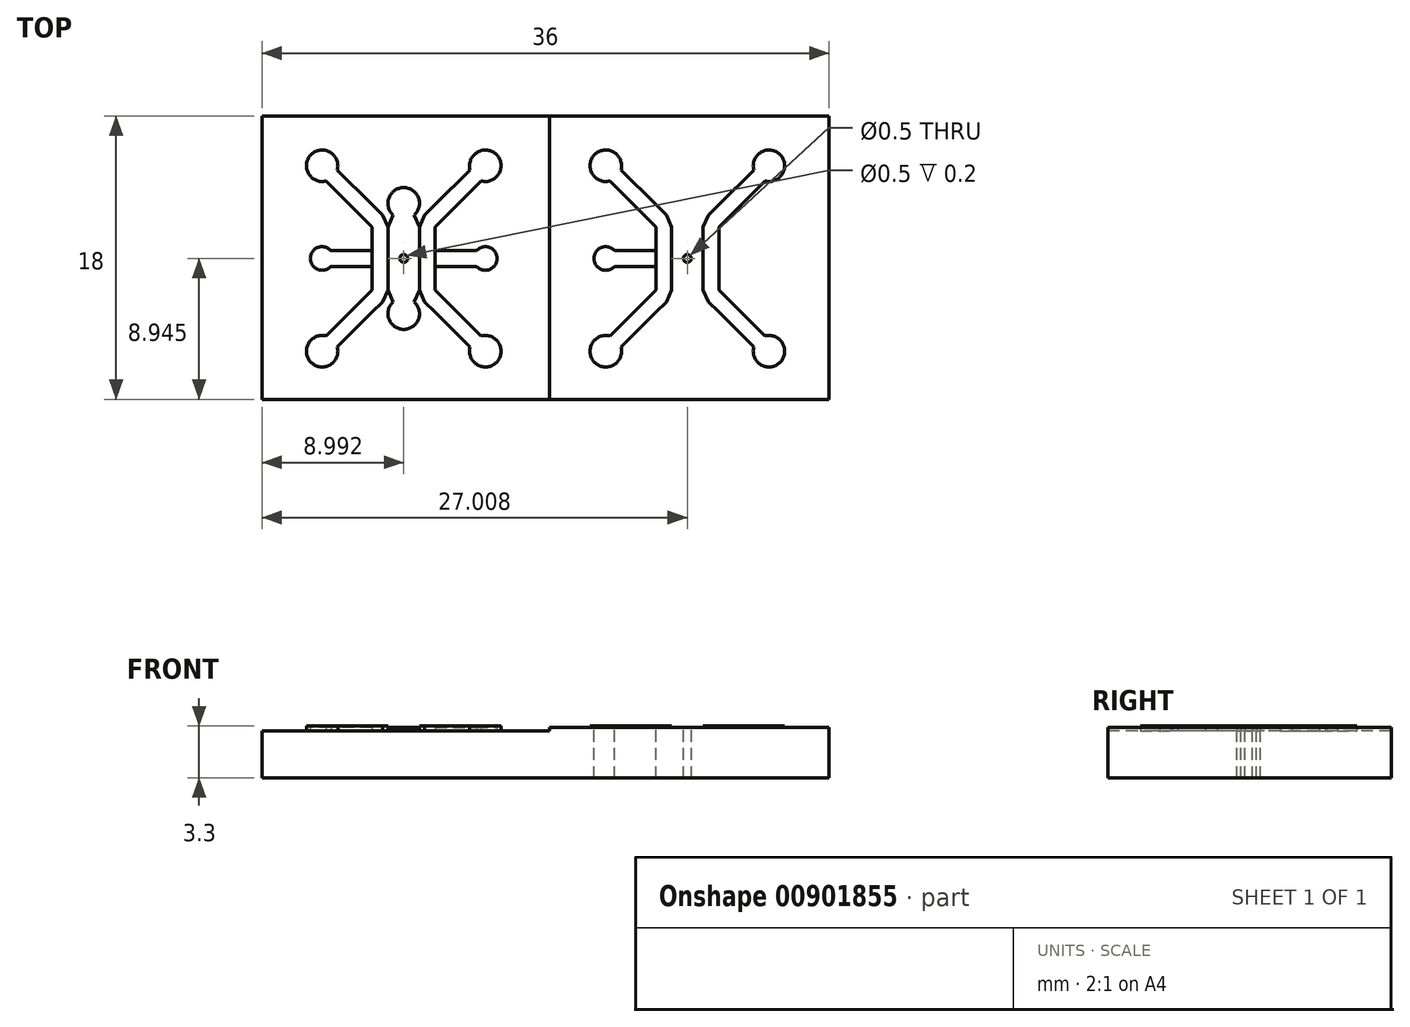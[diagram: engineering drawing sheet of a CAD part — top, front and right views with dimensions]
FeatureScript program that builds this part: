
annotation { "Feature Type Name" : "Feature", "Feature Type Description" : "" }
export const myFeature = defineFeature(function(context is Context, id is Id, definition is map)
    precondition{}
    {
        {
            var Q0;
            Q0=qCreatedBy(makeId("Top.planeOp"),FACE);
            var sketch = newSketch(context, id + "F0", { "sketchPlane" : qUnion([Q0])});
            skLineSegment(sketch, "E0.right", {"start": v(10, 8.95) * mm, "end": v(10, 10.95) * mm});
            skLineSegment(sketch, "E1.MirrorCS", {"start": v(8, 8.95) * mm, "end": v(8, 10.95) * mm});
            skLineSegment(sketch, "E2.MirrorCS", {"start": v(10, 8.95) * mm, "end": v(10, 6.95) * mm});
            skLineSegment(sketch, "E3.MirrorCS", {"start": v(8, 8.95) * mm, "end": v(8, 6.95) * mm});
            skLineSegment(sketch, "E4", {"start": v(9.65, 6.2) * mm, "end": v(10, 6.95) * mm});
            skLineSegment(sketch, "E5", {"start": v(8, 6.95) * mm, "end": v(8.33, 6.2) * mm});
            skCircle(sketch, "E6", {"center": v(9, 8.95) * mm, "radius": 0.25 * mm});
            skArc(sketch, "E7", {"start": v(8.33, 6.2) * mm, "mid": v(9, 4.45) * mm, "end": v(9.65, 6.2) * mm});
            skLineSegment(sketch, "E8.left", {"start": v(10, 10.95) * mm, "end": v(10, 8.95) * mm});
            skLineSegment(sketch, "E8.right", {"start": v(11, 10.95) * mm, "end": v(11, 8.95) * mm});
            skLineSegment(sketch, "E9.MirrorCS", {"start": v(11, 6.95) * mm, "end": v(11, 8.95) * mm});
            skLineSegment(sketch, "E10", {"start": v(10, 6.95) * mm, "end": v(10.33, 6.2) * mm});
            skLineSegment(sketch, "E11", {"start": v(10.33, 6.2) * mm, "end": v(11, 5.53) * mm});
            skLineSegment(sketch, "E12", {"start": v(11, 5.53) * mm, "end": v(13.2, 3.32) * mm});
            skArc(sketch, "E13", {"start": v(13.2, 3.32) * mm, "mid": v(14.88, 2.35) * mm, "end": v(13.92, 4.02) * mm});
            skArc(sketch, "E14.MirrorCS", {"start": v(8.33, 11.7) * mm, "mid": v(9, 13.45) * mm, "end": v(9.65, 11.7) * mm});
            skLineSegment(sketch, "E15.MirrorCS", {"start": v(9.65, 11.7) * mm, "end": v(10, 10.95) * mm});
            skLineSegment(sketch, "E16.MirrorCS", {"start": v(8, 10.95) * mm, "end": v(8.33, 11.7) * mm});
            skLineSegment(sketch, "E17.MirrorCS", {"start": v(10, 10.95) * mm, "end": v(10.33, 11.7) * mm});
            skLineSegment(sketch, "E18.MirrorCS", {"start": v(10.33, 11.7) * mm, "end": v(11, 12.36) * mm});
            skLineSegment(sketch, "E19.MirrorCS", {"start": v(11, 12.36) * mm, "end": v(13.2, 14.58) * mm});
            skArc(sketch, "E20.MirrorCS", {"start": v(13.2, 14.58) * mm, "mid": v(14.88, 15.54) * mm, "end": v(13.92, 13.87) * mm});
            skLineSegment(sketch, "E21", {"start": v(11, 6.95) * mm, "end": v(13.92, 4.02) * mm});
            skLineSegment(sketch, "E22.MirrorCS", {"start": v(11, 10.95) * mm, "end": v(13.92, 13.87) * mm});
            skLineSegment(sketch, "E23.MirrorCS", {"start": v(8, 10.95) * mm, "end": v(7.65, 11.7) * mm});
            skLineSegment(sketch, "E24.MirrorCS", {"start": v(8, 6.95) * mm, "end": v(7.65, 6.2) * mm});
            skLineSegment(sketch, "E25.MirrorCS", {"start": v(7.65, 11.7) * mm, "end": v(7, 12.36) * mm});
            skLineSegment(sketch, "E26.MirrorCS", {"start": v(7, 12.36) * mm, "end": v(4.78, 14.58) * mm});
            skArc(sketch, "E27.MirrorCS", {"start": v(4.78, 14.58) * mm, "mid": v(3.1, 15.54) * mm, "end": v(4.07, 13.87) * mm});
            skLineSegment(sketch, "E28.MirrorCS", {"start": v(7, 10.95) * mm, "end": v(4.07, 13.87) * mm});
            skLineSegment(sketch, "E29.MirrorCS", {"start": v(7, 10.95) * mm, "end": v(7, 8.95) * mm});
            skLineSegment(sketch, "E30.MirrorCS", {"start": v(7, 6.95) * mm, "end": v(7, 8.95) * mm});
            skArc(sketch, "E31.MirrorCS", {"start": v(4.78, 3.32) * mm, "mid": v(3.1, 2.35) * mm, "end": v(4.07, 4.02) * mm});
            skLineSegment(sketch, "E32.MirrorCS", {"start": v(7, 6.95) * mm, "end": v(4.07, 4.02) * mm});
            skLineSegment(sketch, "E33.MirrorCS", {"start": v(7, 5.53) * mm, "end": v(4.78, 3.32) * mm});
            skLineSegment(sketch, "E34.MirrorCS", {"start": v(7.65, 6.2) * mm, "end": v(7, 5.53) * mm});
            skLineSegment(sketch, "E35", {"start": v(11, 9.45) * mm, "end": v(13.61, 9.45) * mm});
            skLineSegment(sketch, "E36", {"start": v(11, 8.45) * mm, "end": v(13.61, 8.45) * mm});
            skArc(sketch, "E37", {"start": v(13.8, 9.6) * mm, "mid": v(13.7, 9.53) * mm, "end": v(13.61, 9.45) * mm});
            skArc(sketch, "E38", {"start": v(13.61, 8.45) * mm, "mid": v(14.91, 8.82) * mm, "end": v(13.8, 9.6) * mm});
            skLineSegment(sketch, "E39.MirrorCS", {"start": v(7, 9.45) * mm, "end": v(4.37, 9.45) * mm});
            skLineSegment(sketch, "E40.MirrorCS", {"start": v(7, 8.45) * mm, "end": v(4.37, 8.45) * mm});
            skArc(sketch, "E41.MirrorCS", {"start": v(4.37, 8.45) * mm, "mid": v(3.07, 8.82) * mm, "end": v(4.18, 9.6) * mm});
            skArc(sketch, "E42.MirrorCS", {"start": v(4.18, 9.6) * mm, "mid": v(4.28, 9.53) * mm, "end": v(4.37, 9.45) * mm});
            skPoint(sketch, "E43.startSnap0", {"position": v(15, 8.95) * mm});
            skPoint(sketch, "E43.startSnap1", {"position": v(14.91, 8.82) * mm});
            skPoint(sketch, "E43.endSnap0", {"position": v(14.91, 8.82) * mm});
            skPoint(sketch, "E44.visualSharp", {"position": v(0, 18) * mm});
            skPoint(sketch, "E45.visualSharp", {"position": v(0, 0) * mm});
            skLineSegment(sketch, "E46", {"start": v(9, 12.45) * mm, "end": v(9, 5.45) * mm});
            skLineSegment(sketch, "E47.bottom", {"start": v(0, 18) * mm, "end": v(18, 18) * mm});
            skLineSegment(sketch, "E47.top", {"start": v(0, 0) * mm, "end": v(18, 0) * mm});
            skLineSegment(sketch, "E47.left", {"start": v(0, 18) * mm, "end": v(0, 0) * mm});
            skLineSegment(sketch, "E47.right", {"start": v(18, 18) * mm, "end": v(18, 0) * mm});
            skLineSegment(sketch, "E48", {"start": v(21.4, 0) * mm, "end": v(21.4, 0) * mm});
            skLineSegment(sketch, "E49.MirrorCS", {"start": v(36, 18) * mm, "end": v(36, 0) * mm});
            skPoint(sketch, "E50.MirrorP", {"position": v(36, 0) * mm});
            skLineSegment(sketch, "E51.MirrorCS", {"start": v(36, 18) * mm, "end": v(18, 18) * mm});
            skPoint(sketch, "E52.MirrorP", {"position": v(36, 18) * mm});
            skLineSegment(sketch, "E53.MirrorCS", {"start": v(14.6, 0) * mm, "end": v(14.6, 0) * mm});
            skLineSegment(sketch, "E54.MirrorCS", {"start": v(36, 0) * mm, "end": v(18, 0) * mm});
            skPoint(sketch, "E55.MirrorP", {"position": v(21.09, 8.82) * mm});
            skLineSegment(sketch, "E56.MirrorCS", {"start": v(28, 10.95) * mm, "end": v(27.67, 11.7) * mm});
            skLineSegment(sketch, "E57.MirrorCS", {"start": v(26, 6.95) * mm, "end": v(25.67, 6.2) * mm});
            skLineSegment(sketch, "E58.MirrorCS", {"start": v(26, 8.95) * mm, "end": v(26, 10.95) * mm});
            skLineSegment(sketch, "E59.MirrorCS", {"start": v(28.35, 6.2) * mm, "end": v(29, 5.53) * mm});
            skArc(sketch, "E60.MirrorCS", {"start": v(31.82, 9.6) * mm, "mid": v(31.72, 9.53) * mm, "end": v(31.63, 9.45) * mm});
            skArc(sketch, "E61.MirrorCS", {"start": v(22.2, 9.6) * mm, "mid": v(22.3, 9.53) * mm, "end": v(22.39, 9.45) * mm});
            skLineSegment(sketch, "E62.MirrorCS", {"start": v(25.67, 11.7) * mm, "end": v(25, 12.36) * mm});
            skLineSegment(sketch, "E63.MirrorCS", {"start": v(28, 10.95) * mm, "end": v(28.35, 11.7) * mm});
            skLineSegment(sketch, "E64.MirrorCS", {"start": v(26, 10.95) * mm, "end": v(25.67, 11.7) * mm});
            skLineSegment(sketch, "E65.MirrorCS", {"start": v(26.35, 11.7) * mm, "end": v(26, 10.95) * mm});
            skLineSegment(sketch, "E66.MirrorCS", {"start": v(28.35, 11.7) * mm, "end": v(29, 12.36) * mm});
            skLineSegment(sketch, "E67.MirrorCS", {"start": v(25.67, 6.2) * mm, "end": v(25, 5.53) * mm});
            skLineSegment(sketch, "E68.MirrorCS", {"start": v(28, 6.95) * mm, "end": v(27.67, 6.2) * mm});
            skLineSegment(sketch, "E69.MirrorCS", {"start": v(28, 6.95) * mm, "end": v(28.35, 6.2) * mm});
            skArc(sketch, "E70.MirrorCS", {"start": v(22.39, 8.45) * mm, "mid": v(21.09, 8.82) * mm, "end": v(22.2, 9.6) * mm});
            skLineSegment(sketch, "E71.MirrorCS", {"start": v(26.35, 6.2) * mm, "end": v(26, 6.95) * mm});
            skPoint(sketch, "E72.MirrorP", {"position": v(21, 8.95) * mm});
            skCircle(sketch, "E73.MirrorC", {"center": v(27, 8.95) * mm, "radius": 0.25 * mm});
            skLineSegment(sketch, "E74.MirrorCS", {"start": v(28, 8.95) * mm, "end": v(28, 10.95) * mm});
            skArc(sketch, "E75.MirrorCS", {"start": v(22.8, 14.58) * mm, "mid": v(21.12, 15.54) * mm, "end": v(22.08, 13.87) * mm});
            skLineSegment(sketch, "E76.MirrorCS", {"start": v(29, 9.45) * mm, "end": v(31.63, 9.45) * mm});
            skLineSegment(sketch, "E77.MirrorCS", {"start": v(29, 6.95) * mm, "end": v(31.93, 4.02) * mm});
            skLineSegment(sketch, "E78.MirrorCS", {"start": v(25, 5.53) * mm, "end": v(22.8, 3.32) * mm});
            skLineSegment(sketch, "E79.MirrorCS", {"start": v(27, 12.45) * mm, "end": v(27, 5.45) * mm});
            skLineSegment(sketch, "E80.MirrorCS", {"start": v(29, 12.36) * mm, "end": v(31.22, 14.58) * mm});
            skLineSegment(sketch, "E81.MirrorCS", {"start": v(29, 6.95) * mm, "end": v(29, 8.95) * mm});
            skLineSegment(sketch, "E82.MirrorCS", {"start": v(29, 5.53) * mm, "end": v(31.22, 3.32) * mm});
            skLineSegment(sketch, "E83.MirrorCS", {"start": v(29, 8.45) * mm, "end": v(31.63, 8.45) * mm});
            skLineSegment(sketch, "E84.MirrorCS", {"start": v(29, 10.95) * mm, "end": v(29, 8.95) * mm});
            skLineSegment(sketch, "E85.MirrorCS", {"start": v(25, 12.36) * mm, "end": v(22.8, 14.58) * mm});
            skLineSegment(sketch, "E86.MirrorCS", {"start": v(26, 10.95) * mm, "end": v(26, 8.95) * mm});
            skArc(sketch, "E87.MirrorCS", {"start": v(31.63, 8.45) * mm, "mid": v(32.93, 8.82) * mm, "end": v(31.82, 9.6) * mm});
            skLineSegment(sketch, "E88.MirrorCS", {"start": v(29, 10.95) * mm, "end": v(31.93, 13.87) * mm});
            skLineSegment(sketch, "E89.MirrorCS", {"start": v(28, 8.95) * mm, "end": v(28, 6.95) * mm});
            skLineSegment(sketch, "E90.MirrorCS", {"start": v(25, 6.95) * mm, "end": v(25, 8.95) * mm});
            skArc(sketch, "E91.MirrorCS", {"start": v(22.8, 3.32) * mm, "mid": v(21.12, 2.35) * mm, "end": v(22.08, 4.02) * mm});
            skLineSegment(sketch, "E92.MirrorCS", {"start": v(25, 10.95) * mm, "end": v(22.08, 13.87) * mm});
            skArc(sketch, "E93.MirrorCS", {"start": v(31.22, 14.58) * mm, "mid": v(32.9, 15.54) * mm, "end": v(31.93, 13.87) * mm});
            skLineSegment(sketch, "E94.MirrorCS", {"start": v(26, 8.95) * mm, "end": v(26, 6.95) * mm});
            skArc(sketch, "E95.MirrorCS", {"start": v(31.22, 3.32) * mm, "mid": v(32.9, 2.35) * mm, "end": v(31.93, 4.02) * mm});
            skLineSegment(sketch, "E96.MirrorCS", {"start": v(25, 10.95) * mm, "end": v(25, 8.95) * mm});
            skArc(sketch, "E97.MirrorCS", {"start": v(27.67, 11.7) * mm, "mid": v(27, 13.45) * mm, "end": v(26.35, 11.7) * mm});
            skLineSegment(sketch, "E98.MirrorCS", {"start": v(25, 8.45) * mm, "end": v(22.39, 8.45) * mm});
            skLineSegment(sketch, "E99.MirrorCS", {"start": v(25, 9.45) * mm, "end": v(22.39, 9.45) * mm});
            skLineSegment(sketch, "E100.MirrorCS", {"start": v(25, 6.95) * mm, "end": v(22.08, 4.02) * mm});
            skArc(sketch, "E101.MirrorCS", {"start": v(27.67, 6.2) * mm, "mid": v(27, 4.45) * mm, "end": v(26.35, 6.2) * mm});
            skLineSegment(sketch, "E102", {"start": v(17.75, 18) * mm, "end": v(17.75, 0) * mm});
            skLineSegment(sketch, "E103.MirrorCS", {"start": v(18.25, 18) * mm, "end": v(18.25, 0) * mm});
            skSolve(sketch);
        }
        {
            var Q0;
            {var subQ0=sQuery(id+"F0.wireOp",EDGE,"E39.MirrorCS");Q0=makeQuery(id+"F0.imprint","IMPRINT",FACE,{"disambiguationData":[TD([[makeQuery(id+"F0.imprint","IMPRINT",EDGE,{"derivedFrom":subQ0}),1.0]])]});}
            var Q1;
            Q1=makeQuery(id+"F0.imprint","IMPRINT",FACE,{"disambiguationData":[TD([[makeQuery(id+"F0.imprint","IMPRINT",EDGE,{"derivedFrom":sQuery(id+"F0.wireOp",EDGE,"E56.MirrorCS")}),1.0]])]});
            var Q2;
            Q2=makeQuery(id+"F0.imprint","IMPRINT",FACE,{"disambiguationData":[TD([[makeQuery(id+"F0.imprint","IMPRINT",EDGE,{"derivedFrom":sQuery(id+"F0.wireOp",EDGE,"E4")}),-1.0]])]});
            var Q3;
            Q3=makeQuery(id+"F0.imprint","IMPRINT",FACE,{"disambiguationData":[TD([[makeQuery(id+"F0.imprint","IMPRINT",EDGE,{"derivedFrom":sQuery(id+"F0.wireOp",EDGE,"E60.MirrorCS")}),1.0]])]});
            var Q4;
            Q4=makeQuery(id+"F0.imprint","IMPRINT",FACE,{"disambiguationData":[TD([[makeQuery(id+"F0.imprint","IMPRINT",EDGE,{"derivedFrom":sQuery(id+"F0.wireOp",EDGE,"E61.MirrorCS")}),-1.0]])]});
            var Q5;
            Q5=makeQuery(id+"F0.imprint","IMPRINT",FACE,{"disambiguationData":[TD([[makeQuery(id+"F0.imprint","IMPRINT",EDGE,{"derivedFrom":sQuery(id+"F0.wireOp",EDGE,"E57.MirrorCS")}),-1.0]])]});
            var Q6;
            {var subQ1=sQuery(id+"F0.wireOp",EDGE,"E49.MirrorCS");Q6=makeQuery(id+"F0.imprint","IMPRINT",FACE,{"disambiguationData":[TD([[makeQuery(id+"F0.imprint","IMPRINT",EDGE,{"derivedFrom":subQ1}),-1.0]])]});}
            var Q7;
            Q7=makeQuery(id+"F0.imprint","IMPRINT",FACE,{"disambiguationData":[TD([[makeQuery(id+"F0.imprint","IMPRINT",EDGE,{"derivedFrom":sQuery(id+"F0.wireOp",EDGE,"E59.MirrorCS")}),1.0]])]});
            var Q8;
            Q8=makeQuery(id+"F0.imprint","IMPRINT",FACE,{"disambiguationData":[TD([[makeQuery(id+"F0.imprint","IMPRINT",EDGE,{"derivedFrom":sQuery(id+"F0.wireOp",EDGE,"E1.MirrorCS")}),1.0]])]});
            var Q9;
            Q9=makeQuery(id+"F0.imprint","IMPRINT",FACE,{"disambiguationData":[TD([[makeQuery(id+"F0.imprint","IMPRINT",EDGE,{"derivedFrom":sQuery(id+"F0.wireOp",EDGE,"E2.MirrorCS")}),1.0]])]});
            var Q10;
            Q10=makeQuery(id+"F0.imprint","IMPRINT",FACE,{"disambiguationData":[TD([[makeQuery(id+"F0.imprint","IMPRINT",EDGE,{"derivedFrom":sQuery(id+"F0.wireOp",EDGE,"E1.MirrorCS")}),-1.0]])]});
            var Q11;
            {var subQ4=sQuery(id+"F0.wireOp",EDGE,"E35");Q11=makeQuery(id+"F0.imprint","IMPRINT",FACE,{"disambiguationData":[TD([[makeQuery(id+"F0.imprint","IMPRINT",EDGE,{"derivedFrom":subQ4}),-1.0]])]});}
            var Q12;
            {var subQ3=sQuery(id+"F0.wireOp",EDGE,"E102");Q12=makeQuery(id+"F0.imprint","IMPRINT",FACE,{"disambiguationData":[TD([[makeQuery(id+"F0.imprint","IMPRINT",EDGE,{"derivedFrom":subQ3}),1.0]])]});}
            var Q13;
            {var subQ5=sQuery(id+"F0.wireOp",EDGE,"E103.MirrorCS");Q13=makeQuery(id+"F0.imprint","IMPRINT",FACE,{"disambiguationData":[TD([[makeQuery(id+"F0.imprint","IMPRINT",EDGE,{"derivedFrom":subQ5}),-1.0]])]});}
            var Q14;
            {var subQ0=sQuery(id+"F0.wireOp",EDGE,"E46");var subQ1=sQuery(id+"F0.wireOp",EDGE,"E6");var subQ2=makeQuery(id+"F0.imprint","INTERSECT",VERTEX,{"disambiguationData":[OD(0.0)],"derivedFrom":[subQ1,subQ0]});Q14=makeQuery(id+"F0.imprint","IMPRINT",FACE,{"disambiguationData":[TD([[makeQuery(id+"F0.imprint","IMPRINT",EDGE,{"disambiguationData":[TD([[subQ2,1.0]])],"derivedFrom":subQ1}),1.0]])]});}
            var Q15;
            {var subQ0=sQuery(id+"F0.wireOp",EDGE,"E79.MirrorCS");var subQ1=sQuery(id+"F0.wireOp",EDGE,"E73.MirrorC");var subQ2=makeQuery(id+"F0.imprint","INTERSECT",VERTEX,{"disambiguationData":[OD(0.0)],"derivedFrom":[subQ1,subQ0]});Q15=makeQuery(id+"F0.imprint","IMPRINT",FACE,{"disambiguationData":[TD([[makeQuery(id+"F0.imprint","IMPRINT",EDGE,{"disambiguationData":[TD([[subQ2,1.0]])],"derivedFrom":subQ1}),-1.0]])]});}
            var Q16;
            {var subQ0=sQuery(id+"F0.wireOp",EDGE,"E46");var subQ1=sQuery(id+"F0.wireOp",EDGE,"E6");var subQ2=makeQuery(id+"F0.imprint","INTERSECT",VERTEX,{"disambiguationData":[OD(0.0)],"derivedFrom":[subQ1,subQ0]});Q16=makeQuery(id+"F0.imprint","IMPRINT",FACE,{"disambiguationData":[TD([[makeQuery(id+"F0.imprint","IMPRINT",EDGE,{"disambiguationData":[TD([[subQ2,-1.0]])],"derivedFrom":subQ1}),1.0]])]});}
            var Q17;
            {var subQ0=sQuery(id+"F0.wireOp",EDGE,"E79.MirrorCS");var subQ1=sQuery(id+"F0.wireOp",EDGE,"E73.MirrorC");var subQ2=makeQuery(id+"F0.imprint","INTERSECT",VERTEX,{"disambiguationData":[OD(0.0)],"derivedFrom":[subQ1,subQ0]});Q17=makeQuery(id+"F0.imprint","IMPRINT",FACE,{"disambiguationData":[TD([[makeQuery(id+"F0.imprint","IMPRINT",EDGE,{"disambiguationData":[TD([[subQ2,-1.0]])],"derivedFrom":subQ1}),-1.0]])]});}
            var Q18;
            {var subQ0=sQuery(id+"F0.wireOp",EDGE,"E51.MirrorCS");var subQ1=sQuery(id+"F0.wireOp",EDGE,"E47.bottom");var subQ2=makeQuery(id+"F0.imprint","INTERSECT",VERTEX,{"derivedFrom":[subQ1,sQuery(id+"F0.wireOp",EDGE,"E47.right"),subQ0]});Q18=makeQuery(id+"F0.imprint","IMPRINT",FACE,{"disambiguationData":[TD([[makeQuery(id+"F0.imprint","IMPRINT",EDGE,{"disambiguationData":[TD([[subQ2,1.0]])],"derivedFrom":subQ1}),1.0]])]});}
            var Q19;
            {var subQ0=sQuery(id+"F0.wireOp",EDGE,"E47.right");var subQ3=sQuery(id+"F0.wireOp",EDGE,"8D0ttMVF-N7t8-bLoh-d2Lt-IWmziKVZ8kqY");var subQ5=makeQuery(id+"F0.imprint","INTERSECT",VERTEX,{"derivedFrom":[subQ0,subQ3]});Q19=makeQuery(id+"F0.imprint","IMPRINT",FACE,{"disambiguationData":[TD([[makeQuery(id+"F0.imprint","IMPRINT",EDGE,{"disambiguationData":[TD([[subQ5,1.0]])],"derivedFrom":subQ0}),-1.0]])]});}
            var Q20;
            {var subQ1=sQuery(id+"F0.wireOp",EDGE,"E47.right");var subQ3=sQuery(id+"F0.wireOp",EDGE,"8D0ttMVF-N7t8-bLoh-d2Lt-IWmziKVZ8kqY");var subQ4=makeQuery(id+"F0.imprint","INTERSECT",VERTEX,{"derivedFrom":[subQ1,subQ3]});Q20=makeQuery(id+"F0.imprint","IMPRINT",FACE,{"disambiguationData":[TD([[makeQuery(id+"F0.imprint","IMPRINT",EDGE,{"disambiguationData":[TD([[subQ4,1.0]])],"derivedFrom":subQ1}),1.0]])]});}
            extrude(context, id + "F1", {"entities" : qUnion([Q0, Q1, Q2, Q3, Q4, Q5, Q6, Q7, Q8, Q9, Q10, Q11, Q12, Q13, Q14, Q15, Q16, Q17, Q18, Q19, Q20]), "depth" : -3 * mm, "offsetDistance" : 25 * mm});
        }
        {
            var Q0;
            Q0=makeQuery(id+"F0.imprint","IMPRINT",FACE,{"disambiguationData":[TD([[makeQuery(id+"F0.imprint","IMPRINT",EDGE,{"derivedFrom":sQuery(id+"F0.wireOp",EDGE,"E1.MirrorCS")}),1.0]])]});
            var Q1;
            Q1=makeQuery(id+"F0.imprint","IMPRINT",FACE,{"disambiguationData":[TD([[makeQuery(id+"F0.imprint","IMPRINT",EDGE,{"derivedFrom":sQuery(id+"F0.wireOp",EDGE,"E2.MirrorCS")}),1.0]])]});
            var Q2;
            Q2=makeQuery(id+"F0.imprint","IMPRINT",FACE,{"disambiguationData":[TD([[makeQuery(id+"F0.imprint","IMPRINT",EDGE,{"derivedFrom":sQuery(id+"F0.wireOp",EDGE,"E57.MirrorCS")}),-1.0]])]});
            var Q3;
            Q3=makeQuery(id+"F0.imprint","IMPRINT",FACE,{"disambiguationData":[TD([[makeQuery(id+"F0.imprint","IMPRINT",EDGE,{"derivedFrom":sQuery(id+"F0.wireOp",EDGE,"E59.MirrorCS")}),1.0]])]});
            extrude(context, id + "F2", {"entities" : qUnion([Q0, Q1, Q2, Q3]), "operationType" : NewBodyOperationType.ADD, "depth" : .3 * mm, "offsetDistance" : 25 * mm});
        }
        {
            var Q0;
            Q0=makeQuery(id+"F0.imprint","IMPRINT",FACE,{"disambiguationData":[TD([[makeQuery(id+"F0.imprint","IMPRINT",EDGE,{"derivedFrom":sQuery(id+"F0.wireOp",EDGE,"E1.MirrorCS")}),-1.0]])]});
            var Q1;
            {var subQ4=sQuery(id+"F0.wireOp",EDGE,"E35");Q1=makeQuery(id+"F0.imprint","IMPRINT",FACE,{"disambiguationData":[TD([[makeQuery(id+"F0.imprint","IMPRINT",EDGE,{"derivedFrom":subQ4}),-1.0]])]});}
            var Q2;
            {var subQ0=sQuery(id+"F0.wireOp",EDGE,"E39.MirrorCS");Q2=makeQuery(id+"F0.imprint","IMPRINT",FACE,{"disambiguationData":[TD([[makeQuery(id+"F0.imprint","IMPRINT",EDGE,{"derivedFrom":subQ0}),1.0]])]});}
            var Q3;
            Q3=makeQuery(id+"F0.imprint","IMPRINT",FACE,{"disambiguationData":[TD([[makeQuery(id+"F0.imprint","IMPRINT",EDGE,{"derivedFrom":sQuery(id+"F0.wireOp",EDGE,"E61.MirrorCS")}),-1.0]])]});
            var Q4;
            Q4=makeQuery(id+"F0.imprint","IMPRINT",FACE,{"disambiguationData":[TD([[makeQuery(id+"F0.imprint","IMPRINT",EDGE,{"derivedFrom":sQuery(id+"F0.wireOp",EDGE,"E56.MirrorCS")}),1.0]])]});
            var Q5;
            Q5=makeQuery(id+"F0.imprint","IMPRINT",FACE,{"disambiguationData":[TD([[makeQuery(id+"F0.imprint","IMPRINT",EDGE,{"derivedFrom":sQuery(id+"F0.wireOp",EDGE,"E60.MirrorCS")}),1.0]])]});
            extrude(context, id + "F3", {"entities" : qUnion([Q0, Q1, Q2, Q3, Q4, Q5]), "operationType" : NewBodyOperationType.ADD, "depth" : .2 * mm, "offsetDistance" : 25 * mm});
        }
    });
